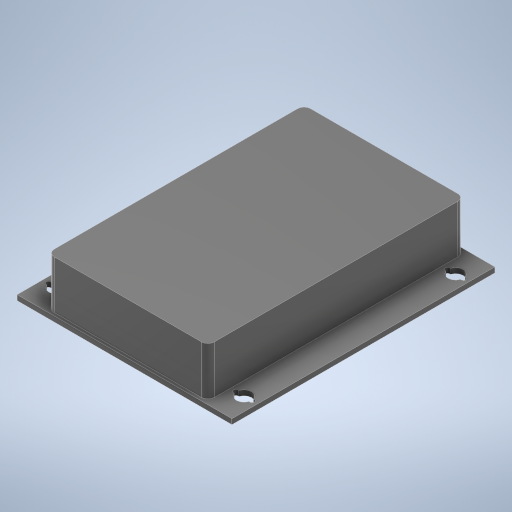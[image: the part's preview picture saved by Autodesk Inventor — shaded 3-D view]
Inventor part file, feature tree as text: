
AUTODESK INVENTOR PART (.ipt)
format: ipt  version: 2024.2 (Build 282272000, 272)  size: 294,400 bytes
history: native  units: mm
features: extrude x2, sketch x1, fillet x1
ambient origin geometry x8: Origin, YZ Plane, XZ Plane, XY Plane, X Axis, Y Axis, Z Axis, Center Point
bodies: Solid1 (feature_tree)
feature tree (4):
  sketch  "Sketch1"  dims[d0=82.0mm d1=67.0mm d7=1.6mm d8=0.0mm d9=16.6mm d10=0.0mm d18=2.0mm d19=4.8mm d30=6.5mm d33=58.5mm d34=66.0mm d36=1.5mm d37=8.5mm d38=1.0mm d41=16.0mm d42=6.5mm d43=1.0mm]
  extrude  "Extrusion1"  Depth=67.0mm
  extrude  "Extrusion2"  Depth=1.6mm TaperAngle=0.0deg
  fillet  "Fillet1"  Radius=16.6mm
